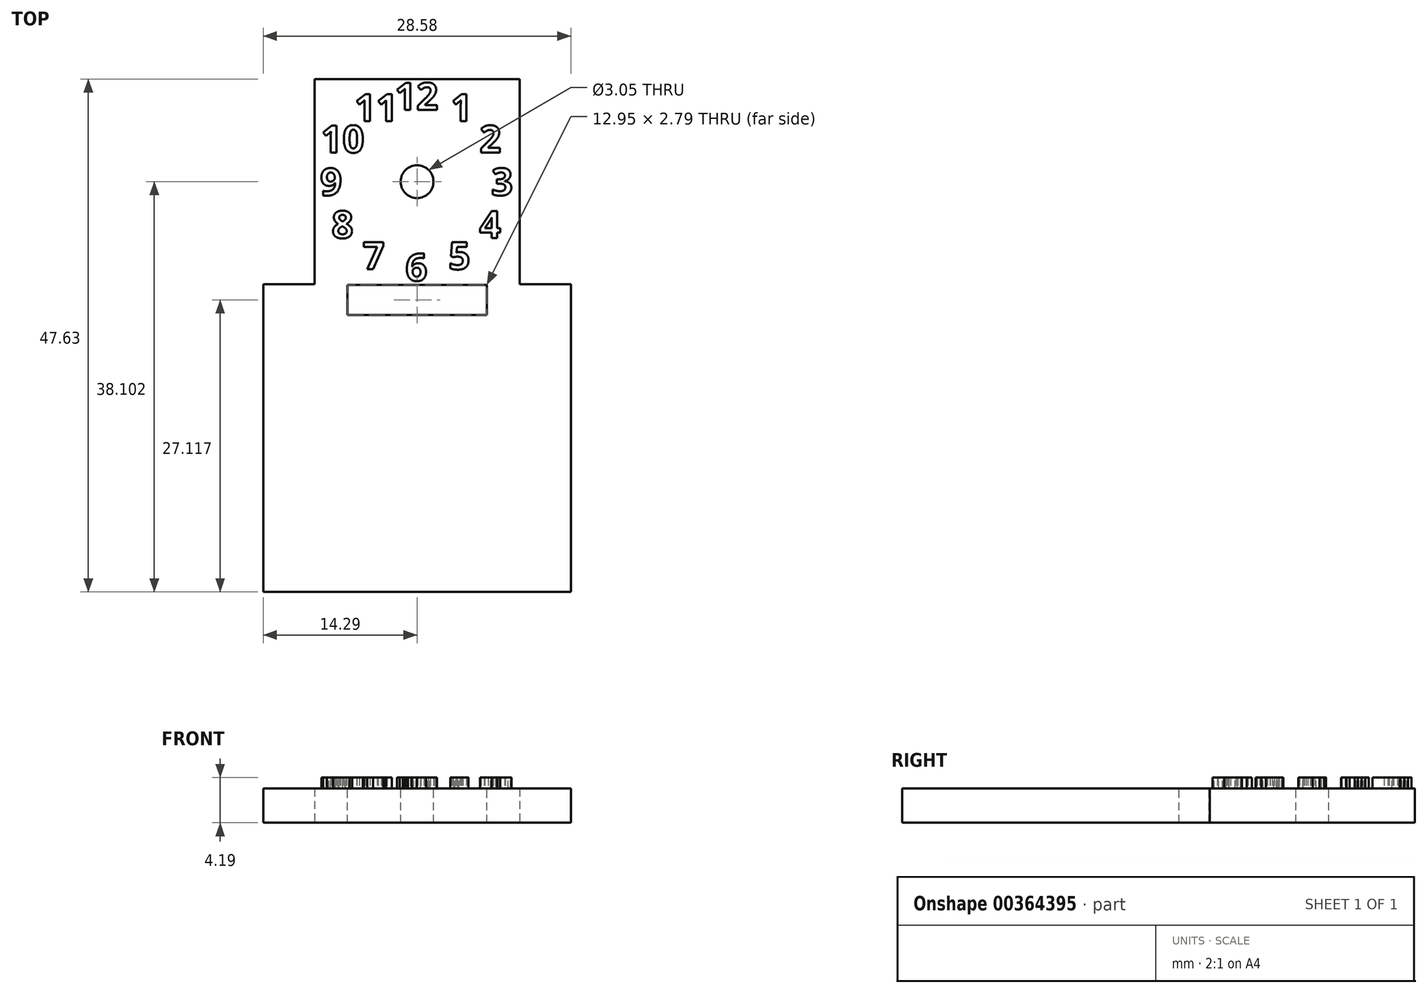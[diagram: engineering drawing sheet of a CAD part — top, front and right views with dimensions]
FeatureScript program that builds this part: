
annotation { "Feature Type Name" : "Feature", "Feature Type Description" : "" }
export const myFeature = defineFeature(function(context is Context, id is Id, definition is map)
    precondition{}
    {
        {
            var Q0;
            Q0=qCreatedBy(makeId("Top.planeOp"),FACE);
            cPlane(context, id + "F0", {"entities" : qUnion([Q0]), "cplaneType" : CPlaneType.OFFSET, "offset" : 0 * mm, "width" : 152.4 * mm, "height" : 152.4 * mm});
        }
        {
            var Q0;
            Q0=qCreatedBy(id+"F0.planeOp",FACE);
            var sketch = newSketch(context, id + "F1", { "sketchPlane" : qUnion([Q0])});
            skLineSegment(sketch, "E0.bottom", {"start": v(-14.29, 14.29) * mm, "end": v(-9.52, 14.29) * mm});
            skLineSegment(sketch, "E0.top", {"start": v(-14.29, -14.29) * mm, "end": v(14.29, -14.29) * mm});
            skLineSegment(sketch, "E0.left", {"start": v(-14.29, 14.29) * mm, "end": v(-14.29, -14.29) * mm});
            skLineSegment(sketch, "E0.right", {"start": v(14.29, 14.29) * mm, "end": v(14.29, -14.29) * mm});
            skLineSegment(sketch, "E1.top", {"start": v(-9.53, 33.34) * mm, "end": v(9.53, 33.34) * mm});
            skLineSegment(sketch, "E1.left", {"start": v(-9.52, 14.29) * mm, "end": v(-9.53, 33.34) * mm});
            skLineSegment(sketch, "E1.right", {"start": v(9.53, 14.29) * mm, "end": v(9.52, 33.34) * mm});
            skLineSegment(sketch, "E2.trimOffspring", {"start": v(9.52, 14.29) * mm, "end": v(14.29, 14.29) * mm});
            skSolve(sketch);
        }
        {
            var Q0;
            Q0=makeQuery(id+"F1.imprint","IMPRINT",FACE,{"disambiguationData":[TD([[makeQuery(id+"F1.imprint","IMPRINT",EDGE,{"derivedFrom":sQuery(id+"F1.wireOp",EDGE,"E0.bottom")}),-1.0]])]});
            extrude(context, id + "F2", {"entities" : qUnion([Q0]), "depth" : 3.17 * mm});
        }
        {
            var Q0;
            Q0=makeQuery(id+"FlI8lcY6gUrTJ5J_2.boolean.opBoolean","SPLIT",FACE,{"disambiguationData":[TD([makeQuery(id+"FmJZvC8EDos19ny_2.opExtrude","SWEPT_FACE",FACE,{"disambiguationData":[OSD([sQuery(id+"FXq9kdwpmuHOact_2.wireOp",EDGE,"BCAx9Tqo-fBlw-zAbO-Tf9r-uVRlVFPoE0ps.bottom")])]})])],"derivedFrom":makeQuery(id+"F2.opExtrude","CAP_FACE",FACE,{"disambiguationData":[OSD([sQuery(id+"F1.wireOp",EDGE,"E0.bottom"),sQuery(id+"F1.wireOp",EDGE,"E0.top"),sQuery(id+"F1.wireOp",EDGE,"E0.left"),sQuery(id+"F1.wireOp",EDGE,"E0.right"),sQuery(id+"F1.wireOp",EDGE,"E1.top"),sQuery(id+"F1.wireOp",EDGE,"E1.left"),sQuery(id+"F1.wireOp",EDGE,"E1.right"),sQuery(id+"F1.wireOp",EDGE,"E2.trimOffspring")])],"isStart":false})});
            var sketch = newSketch(context, id + "F3", { "sketchPlane" : qUnion([Q0])});
            skLineSegment(sketch, "E3.bottom", {"start": v(-6.48, 14.22) * mm, "end": v(6.48, 14.22) * mm});
            skLineSegment(sketch, "E3.top", {"start": v(-6.48, 11.43) * mm, "end": v(6.48, 11.43) * mm});
            skLineSegment(sketch, "E3.left", {"start": v(-6.48, 14.22) * mm, "end": v(-6.48, 11.43) * mm});
            skLineSegment(sketch, "E3.right", {"start": v(6.48, 14.22) * mm, "end": v(6.48, 11.43) * mm});
            skSolve(sketch);
        }
        {
            var Q0;
            Q0=makeQuery(id+"F3.imprint","IMPRINT",FACE,{"disambiguationData":[TD([[makeQuery(id+"F3.imprint","IMPRINT",EDGE,{"derivedFrom":sQuery(id+"F3.wireOp",EDGE,"E3.bottom")}),-1.0]])]});
            extrude(context, id + "F4", {"entities" : qUnion([Q0]), "operationType" : NewBodyOperationType.REMOVE, "oppositeDirection" : true, "depth" : 25.4 * mm});
        }
        {
            var Q0;
            Q0=makeQuery(id+"F2.opExtrude","CAP_FACE",FACE,{"disambiguationData":[OSD([sQuery(id+"F1.wireOp",EDGE,"E0.bottom"),sQuery(id+"F1.wireOp",EDGE,"E0.top"),sQuery(id+"F1.wireOp",EDGE,"E0.left"),sQuery(id+"F1.wireOp",EDGE,"E0.right"),sQuery(id+"F1.wireOp",EDGE,"E1.top"),sQuery(id+"F1.wireOp",EDGE,"E1.left"),sQuery(id+"F1.wireOp",EDGE,"E1.right"),sQuery(id+"F1.wireOp",EDGE,"E2.trimOffspring")])],"isStart":false});
            var sketch = newSketch(context, id + "F5", { "sketchPlane" : qUnion([Q0])});
            skCircle(sketch, "E4", {"center": v(0, 23.81) * mm, "radius": 7.94 * mm, "construction": true});
            skText(sketch, "E5", { "text": "1", "fontName": "OpenSans-Bold.ttf"});
            skLineSegment(sketch, "E6", {"start": v(0, 23.81) * mm, "end": v(0, 31.75) * mm, "construction": true});
            skLineSegment(sketch, "E7.1.0", {"start": v(0, 23.81) * mm, "end": v(-3.97, 30.69) * mm, "construction": true});
            skLineSegment(sketch, "E7.2.0", {"start": v(0, 23.81) * mm, "end": v(-6.87, 27.78) * mm, "construction": true});
            skLineSegment(sketch, "E7.3.0", {"start": v(0, 23.81) * mm, "end": v(-7.94, 23.81) * mm, "construction": true});
            skLineSegment(sketch, "E7.4.0", {"start": v(0, 23.81) * mm, "end": v(-6.87, 19.84) * mm, "construction": true});
            skLineSegment(sketch, "E7.5.0", {"start": v(0, 23.81) * mm, "end": v(-3.97, 16.94) * mm, "construction": true});
            skLineSegment(sketch, "E7.6.0", {"start": v(0, 23.81) * mm, "end": v(0, 15.88) * mm, "construction": true});
            skLineSegment(sketch, "E7.7.0", {"start": v(0, 23.81) * mm, "end": v(3.97, 16.94) * mm, "construction": true});
            skLineSegment(sketch, "E7.8.0", {"start": v(0, 23.81) * mm, "end": v(6.87, 19.84) * mm, "construction": true});
            skLineSegment(sketch, "E7.9.0", {"start": v(0, 23.81) * mm, "end": v(7.94, 23.81) * mm, "construction": true});
            skLineSegment(sketch, "E7.10.0", {"start": v(0, 23.81) * mm, "end": v(6.87, 27.78) * mm, "construction": true});
            skLineSegment(sketch, "E7.11.0", {"start": v(0, 23.81) * mm, "end": v(3.97, 30.69) * mm, "construction": true});
            skLineSegment(sketch, "E8", {"start": v(1.71, 30.69) * mm, "end": v(3.97, 30.69) * mm, "construction": true});
            skText(sketch, "E9", { "text": "2", "fontName": "OpenSans-Bold.ttf"});
            skText(sketch, "E10", { "text": "3", "fontName": "OpenSans-Bold.ttf"});
            skText(sketch, "E11", { "text": "4", "fontName": "OpenSans-Bold.ttf"});
            skText(sketch, "E12", { "text": "5", "fontName": "OpenSans-Bold.ttf"});
            skText(sketch, "E13", { "text": "6", "fontName": "OpenSans-Bold.ttf"});
            skText(sketch, "E14", { "text": "7", "fontName": "OpenSans-Bold.ttf"});
            skText(sketch, "E15", { "text": "8", "fontName": "OpenSans-Bold.ttf"});
            skText(sketch, "E16", { "text": "9", "fontName": "OpenSans-Bold.ttf"});
            skText(sketch, "E17", { "text": "12", "fontName": "OpenSans-Bold.ttf"});
            skLineSegment(sketch, "E18", {"start": v(0, 31.75) * mm, "end": v(5.72, 31.75) * mm, "construction": true});
            skLineSegment(sketch, "E19", {"start": v(-3.97, 30.69) * mm, "end": v(-1.3, 30.69) * mm, "construction": true});
            skLineSegment(sketch, "E20", {"start": v(-6.87, 27.78) * mm, "end": v(-1.95, 27.78) * mm, "construction": true});
            skLineSegment(sketch, "E21", {"start": v(-6.87, 19.84) * mm, "end": v(-3.8, 19.84) * mm, "construction": true});
            skLineSegment(sketch, "E22", {"start": v(-3.97, 16.94) * mm, "end": v(0.1, 16.94) * mm, "construction": true});
            skLineSegment(sketch, "E23", {"start": v(0, 15.88) * mm, "end": v(4.68, 15.88) * mm, "construction": true});
            skText(sketch, "E24", { "text": "11", "fontName": "OpenSans-Bold.ttf"});
            skText(sketch, "E25", { "text": "10", "fontName": "OpenSans-Bold.ttf"});
            const initialGuessF5  = {"E5": [0.00313, 0.02942, 1, 0, 0.00254], "E9": [0.0058, 0.02651, 1, 0, 0.00254], "E10": [0.00688, 0.02254, 1, 0, 0.00254], "E11": [0.00578, 0.01857, 1, 0, 0.00254], "E12": [0.00293, 0.01567, 1, 0, 0.00254], "E13": [-0.00107, 0.0146, 1, 0, 0.00254], "E14": [-0.00503, 0.01567, 1, 0, 0.00254], "E15": [-0.00793, 0.01857, 1, 0, 0.00254], "E16": [-0.009, 0.02254, 1, 0, 0.00254], "E17": [-0.00207, 0.03048, 1, 0, 0.00254], "E24": [-0.00582, 0.02942, 1, 0, 0.00254], "E25": [-0.00894, 0.02651, 1, 0, 0.00254]};
            skSetInitialGuess(sketch, initialGuessF5);
            skSolve(sketch);
        }
        {
            var Q0;
            Q0 = qSketchRegion(id + "F5", true);
            extrude(context, id + "F6", {"entities" : qUnion([Q0]), "operationType" : NewBodyOperationType.ADD, "depth" : 1.02 * mm});
        }
        {
            var Q0;
            Q0=makeQuery(id+"F5.imprint","IMPRINT",FACE,{"disambiguationData":[TD([[makeQuery(id+"F5.imprint","IMPRINT",EDGE,{"derivedFrom":sQuery(id+"F5.wireOp",EDGE,"E5.sketch_text.stroke-0")}),1.0]])]});
            var sketch = newSketch(context, id + "F7", { "sketchPlane" : qUnion([Q0])});
            skCircle(sketch, "E26", {"center": v(0, 23.81) * mm, "radius": 1.52 * mm});
            skSolve(sketch);
        }
        {
            var Q0;
            Q0=makeQuery(id+"F7.imprint","IMPRINT",FACE,{"disambiguationData":[TD([[makeQuery(id+"F7.imprint","IMPRINT",EDGE,{"derivedFrom":sQuery(id+"F7.wireOp",EDGE,"E26")}),1.0]])]});
            extrude(context, id + "F8", {"entities" : qUnion([Q0]), "operationType" : NewBodyOperationType.REMOVE, "endBound" : BoundingType.UP_TO_NEXT, "oppositeDirection" : true, "depth" : 25.4 * mm});
        }
    });
